# Revit family: Table-Teknion-CFTBKE-Figure_Table_Butter_Knife_Edge-V_Enclosed_Leg_Base-R2023
name_source: partatom
category: Furniture
units: mm (PartAtom-declared; Revit-internal decimal feet)

## family parameters
Always vertical = Yes
Cut with Voids When Loaded = No
Enable Cutting in Views = No
OmniClass Number = 23.40.20.00
OmniClass Title = General Furniture and Specialties
Render Appearance Source = Family Geometry
Room Calculation Point = No
Shared = Yes
Work Plane-Based = No

## types (3) — shared parameters
Assembly Code = E2020200
Description = Figure Table, Rectangular, Enclosed V-Leg, Butter Knife Edge
Manufacturer = Teknion
Manufacturer Fax = 416.661.4586
Part Number = CTFBKE
Product Documentation Link = https://d2r72yk5wmppdj.cloudfront.net
Product Line = Figure Table
Product Page URL = https://www.teknion.com
Series = Custom Wood Boardroom & Reception Tables
Sustainability Data = https://www.teknion.com
URL = www.teknion.com
Unit Weight URL = http://www.teknion.com
Warranty = http://www.teknion.com
zero-valued in all types: Default Elevation

## per-type parameters (varying)
| type | Depth | Dim 4 | Model |
| 60" Depth | 60 " | 8.346 " | CTFBKE60____ |
| 54" Depth | 54 " | 6.846 " | CTFBKE54____ |
| 48" Depth | 48 " | 6.846 " | CTFBKE48____ |

## geometry (parser evidence)
native form markers: Sweep x12
no freeform markers — native parametric forms only
